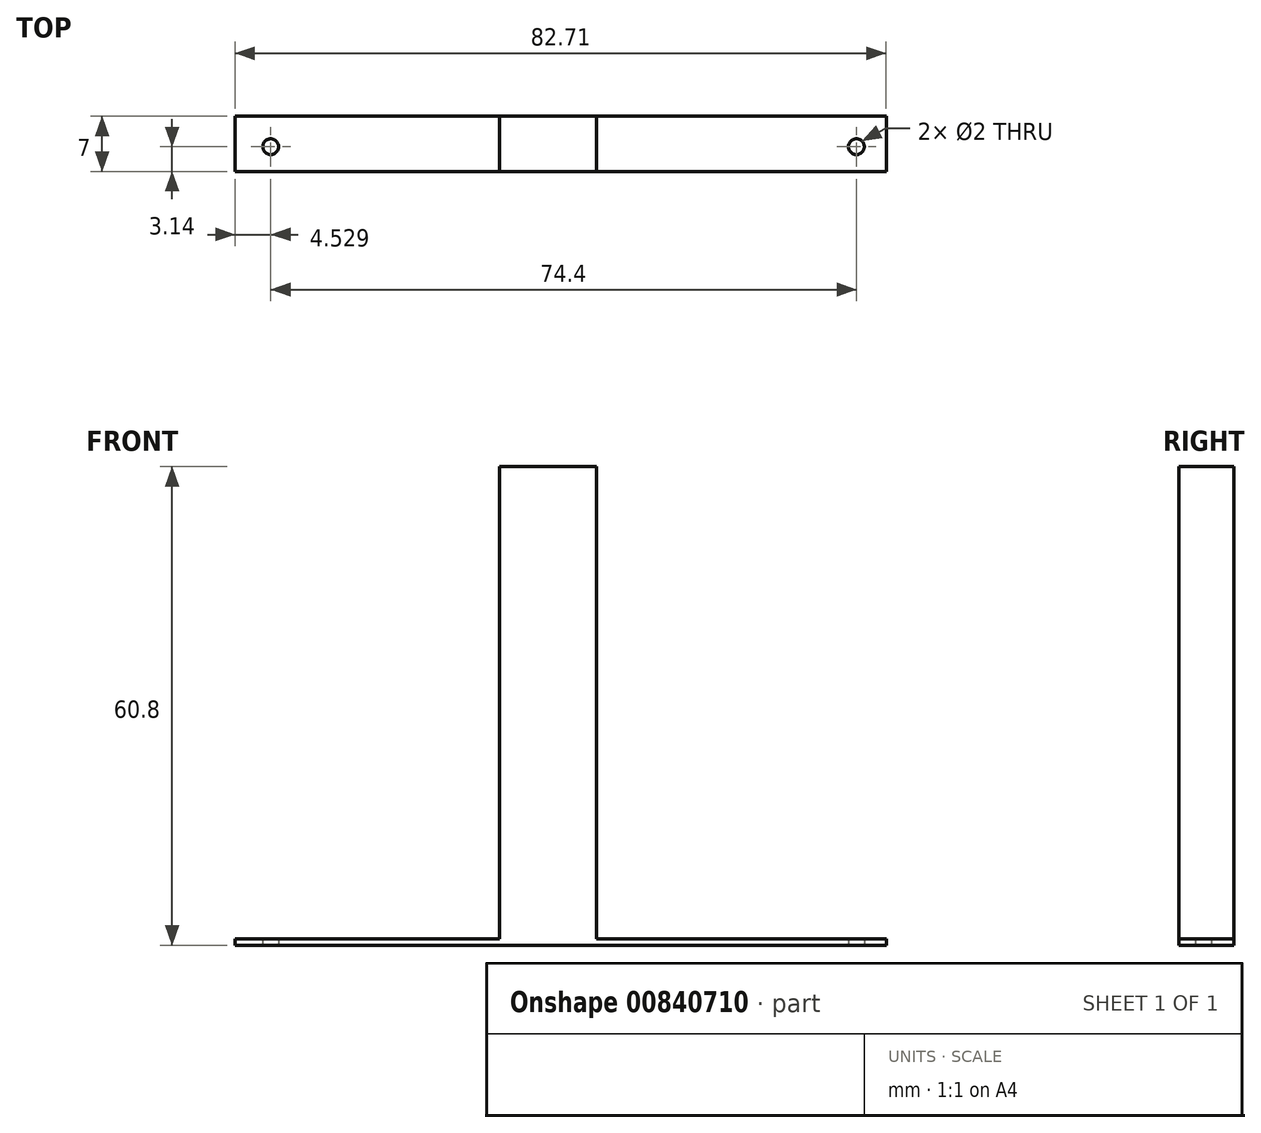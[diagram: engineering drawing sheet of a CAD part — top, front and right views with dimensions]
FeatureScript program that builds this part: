
annotation { "Feature Type Name" : "Feature", "Feature Type Description" : "" }
export const myFeature = defineFeature(function(context is Context, id is Id, definition is map)
    precondition{}
    {
        {
            var Q0;
            Q0=qCreatedBy(makeId("Top.planeOp"),FACE);
            var sketch = newSketch(context, id + "F0", { "sketchPlane" : qUnion([Q0])});
            skLineSegment(sketch, "E0.bottom", {"start": v(-39.85, 3.86) * mm, "end": v(42.86, 3.86) * mm});
            skLineSegment(sketch, "E0.top", {"start": v(-39.85, -3.14) * mm, "end": v(42.86, -3.14) * mm});
            skLineSegment(sketch, "E0.left", {"start": v(-39.85, 3.86) * mm, "end": v(-39.85, -3.14) * mm});
            skLineSegment(sketch, "E0.right", {"start": v(42.86, 3.86) * mm, "end": v(42.86, -3.14) * mm});
            skCircle(sketch, "E1", {"center": v(-35.32, 0) * mm, "radius": 1 * mm});
            skCircle(sketch, "E2", {"center": v(39.08, 0) * mm, "radius": 1 * mm});
            skSolve(sketch);
        }
        {
            var Q0;
            Q0=makeQuery(id+"F0.imprint","IMPRINT",FACE,{"disambiguationData":[TD([[makeQuery(id+"F0.imprint","IMPRINT",EDGE,{"derivedFrom":sQuery(id+"F0.wireOp",EDGE,"E0.bottom")}),-1.0]])]});
            extrude(context, id + "F1", {"entities" : qUnion([Q0]), "depth" : .8 * mm, "offsetDistance" : 25 * mm});
        }
        {
            var Q0;
            Q0=makeQuery(id+"F1.opExtrude","CAP_FACE",FACE,{"disambiguationData":[OSD([sQuery(id+"F0.wireOp",EDGE,"E0.bottom"),sQuery(id+"F0.wireOp",EDGE,"E0.top"),sQuery(id+"F0.wireOp",EDGE,"E0.left"),sQuery(id+"F0.wireOp",EDGE,"E0.right"),sQuery(id+"F0.wireOp",EDGE,"E1"),sQuery(id+"F0.wireOp",EDGE,"E2")])],"isStart":false});
            var sketch = newSketch(context, id + "F2", { "sketchPlane" : qUnion([Q0])});
            skLineSegment(sketch, "E3.bottom", {"start": v(-6.29, 3.86) * mm, "end": v(6.09, 3.86) * mm});
            skLineSegment(sketch, "E3.top", {"start": v(-6.29, -3.14) * mm, "end": v(6.09, -3.14) * mm});
            skLineSegment(sketch, "E3.left", {"start": v(-6.29, 3.86) * mm, "end": v(-6.29, -3.14) * mm});
            skLineSegment(sketch, "E3.right", {"start": v(6.09, 3.86) * mm, "end": v(6.09, -3.14) * mm});
            skSolve(sketch);
        }
        {
            var Q0;
            Q0 = qSketchRegion(id + "F2", true);
            extrude(context, id + "F3", {"entities" : qUnion([Q0]), "operationType" : NewBodyOperationType.ADD, "depth" : 60 * mm, "offsetDistance" : 25 * mm});
        }
    });
